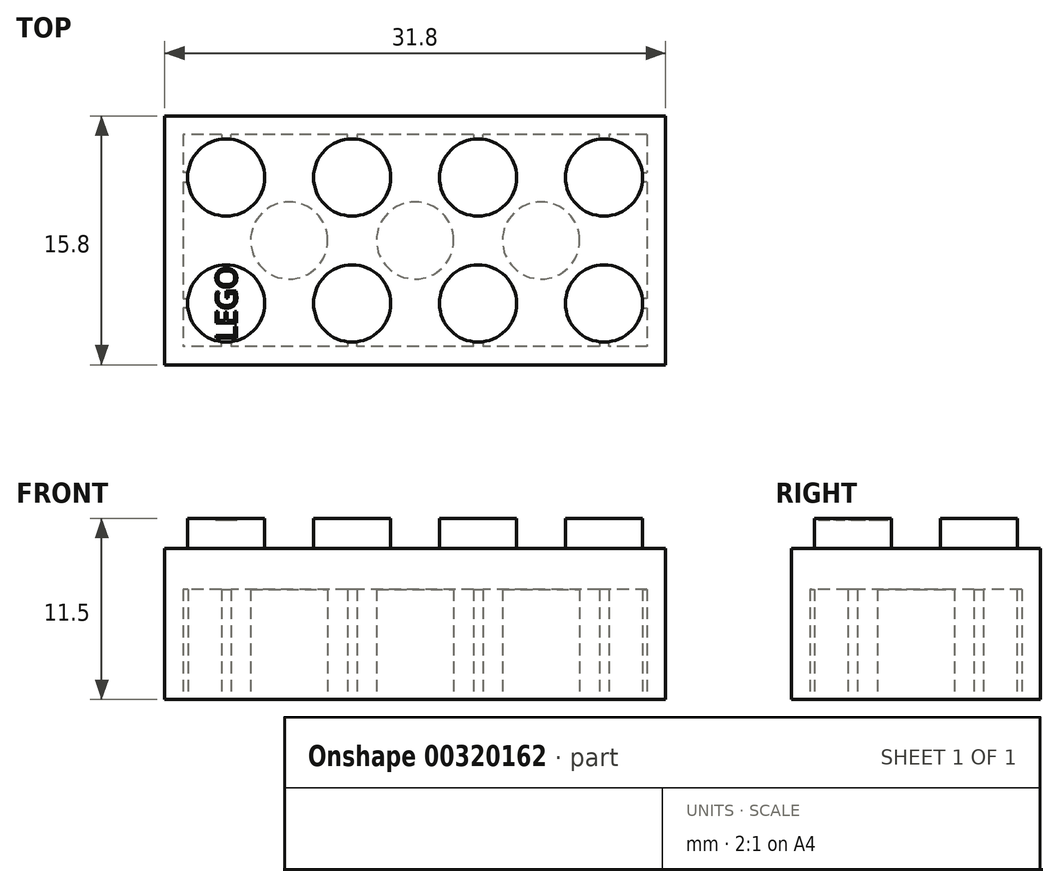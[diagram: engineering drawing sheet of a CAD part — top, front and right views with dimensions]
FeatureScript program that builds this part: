
annotation { "Feature Type Name" : "Feature", "Feature Type Description" : "" }
export const myFeature = defineFeature(function(context is Context, id is Id, definition is map)
    precondition{}
    {
        {
            var Q0;
            Q0=qCreatedBy(makeId("Top.planeOp"),FACE);
            var sketch = newSketch(context, id + "F0", { "sketchPlane" : qUnion([Q0])});
            skLineSegment(sketch, "E0.bottom", {"start": v(0, 0) * mm, "end": v(31.8, 0) * mm});
            skLineSegment(sketch, "E0.top", {"start": v(0, 15.8) * mm, "end": v(31.8, 15.8) * mm});
            skLineSegment(sketch, "E0.left", {"start": v(0, 0) * mm, "end": v(0, 15.8) * mm});
            skLineSegment(sketch, "E0.right", {"start": v(31.8, 0) * mm, "end": v(31.8, 15.8) * mm});
            skCircle(sketch, "E1", {"center": v(3.9, 11.9) * mm, "radius": 1.3 * mm, "construction": true});
            skLineSegment(sketch, "E2.bottom", {"start": v(-0.1, 15.9) * mm, "end": v(31.9, 15.9) * mm, "construction": true});
            skLineSegment(sketch, "E2.top", {"start": v(-0.1, -0.1) * mm, "end": v(31.9, -0.1) * mm, "construction": true});
            skLineSegment(sketch, "E2.left", {"start": v(-0.1, 15.9) * mm, "end": v(-0.1, -0.1) * mm, "construction": true});
            skLineSegment(sketch, "E2.right", {"start": v(31.9, 15.9) * mm, "end": v(31.9, -0.1) * mm, "construction": true});
            skLineSegment(sketch, "E3", {"start": v(15.5, 15.9) * mm, "end": v(15.5, -0.1) * mm, "construction": true});
            skLineSegment(sketch, "E4", {"start": v(16.3, -0.1) * mm, "end": v(16.3, 15.9) * mm, "construction": true});
            skLineSegment(sketch, "E5", {"start": v(15.5, 7.9) * mm, "end": v(16.3, 7.9) * mm, "construction": true});
            skCircle(sketch, "E6", {"center": v(15.9, 7.9) * mm, "radius": 3.2 * mm, "construction": true});
            skPoint(sketch, "E7", {"position": v(15.9, -0.1) * mm});
            skLineSegment(sketch, "E8", {"start": v(31.8, 7.9) * mm, "end": v(31.9, 7.9) * mm, "construction": true});
            skLineSegment(sketch, "E9", {"start": v(15.9, 15.9) * mm, "end": v(15.9, 15.8) * mm, "construction": true});
            skCircle(sketch, "E10", {"center": v(15.9, 7.9) * mm, "radius": 2.45 * mm, "construction": true});
            skCircle(sketch, "E11", {"center": v(3.9, 11.9) * mm, "radius": 2.45 * mm, "construction": true});
            skLineSegment(sketch, "E12", {"start": v(7.9, 15.9) * mm, "end": v(7.9, 7.9) * mm, "construction": true});
            skLineSegment(sketch, "E13", {"start": v(23.9, 15.9) * mm, "end": v(23.9, -0.1) * mm, "construction": true});
            skLineSegment(sketch, "E14", {"start": v(-0.1, 7.9) * mm, "end": v(7.9, 7.9) * mm, "construction": true});
            skLineSegment(sketch, "E15", {"start": v(7.9, 7.9) * mm, "end": v(15.9, 7.9) * mm, "construction": true});
            skLineSegment(sketch, "E16", {"start": v(23.9, 7.9) * mm, "end": v(15.9, 7.9) * mm, "construction": true});
            skLineSegment(sketch, "E17", {"start": v(23.9, 7.9) * mm, "end": v(31.9, 7.9) * mm, "construction": true});
            skPoint(sketch, "E18", {"position": v(0, 7.9) * mm});
            skPoint(sketch, "E19", {"position": v(3.9, 7.9) * mm});
            skLineSegment(sketch, "E20", {"start": v(7.9, 7.9) * mm, "end": v(7.9, -0.1) * mm, "construction": true});
            skPoint(sketch, "E21", {"position": v(7.9, 11.9) * mm});
            skCircle(sketch, "E22", {"center": v(7.9, 7.9) * mm, "radius": 3.2 * mm, "construction": true});
            skCircle(sketch, "E23", {"center": v(7.9, 7.9) * mm, "radius": 2.45 * mm, "construction": true});
            skCircle(sketch, "E24", {"center": v(23.9, 7.9) * mm, "radius": 3.2 * mm, "construction": true});
            skCircle(sketch, "E25", {"center": v(23.9, 7.9) * mm, "radius": 2.45 * mm, "construction": true});
            skLineSegment(sketch, "E26.bottom", {"start": v(30.63, 14.63) * mm, "end": v(1.17, 14.63) * mm, "construction": true});
            skLineSegment(sketch, "E26.top", {"start": v(30.63, 1.17) * mm, "end": v(1.17, 1.17) * mm, "construction": true});
            skLineSegment(sketch, "E26.left", {"start": v(30.63, 14.63) * mm, "end": v(30.63, 1.17) * mm, "construction": true});
            skLineSegment(sketch, "E26.right", {"start": v(1.17, 14.63) * mm, "end": v(1.17, 1.17) * mm, "construction": true});
            skLineSegment(sketch, "E27", {"start": v(3.6, 14.63) * mm, "end": v(3.6, 14.33) * mm, "construction": true});
            skLineSegment(sketch, "E28", {"start": v(3.6, 14.33) * mm, "end": v(4.2, 14.33) * mm, "construction": true});
            skLineSegment(sketch, "E29", {"start": v(4.2, 14.33) * mm, "end": v(4.2, 14.63) * mm, "construction": true});
            skLineSegment(sketch, "E30", {"start": v(1.17, 11.6) * mm, "end": v(1.47, 11.6) * mm, "construction": true});
            skLineSegment(sketch, "E31", {"start": v(1.47, 11.6) * mm, "end": v(1.47, 12.2) * mm, "construction": true});
            skLineSegment(sketch, "E32", {"start": v(1.47, 12.2) * mm, "end": v(1.17, 12.2) * mm, "construction": true});
            skCircle(sketch, "E33.MirrorC", {"center": v(11.9, 11.9) * mm, "radius": 2.45 * mm, "construction": true});
            skCircle(sketch, "E34.MirrorC", {"center": v(11.9, 11.9) * mm, "radius": 1.3 * mm, "construction": true});
            skCircle(sketch, "E35.MirrorC", {"center": v(3.9, 3.9) * mm, "radius": 2.45 * mm, "construction": true});
            skCircle(sketch, "E36.MirrorC", {"center": v(3.9, 3.9) * mm, "radius": 1.3 * mm, "construction": true});
            skCircle(sketch, "E37.MirrorC", {"center": v(11.9, 3.9) * mm, "radius": 2.45 * mm, "construction": true});
            skCircle(sketch, "E38.MirrorC", {"center": v(11.9, 3.9) * mm, "radius": 1.3 * mm, "construction": true});
            skLineSegment(sketch, "E39", {"start": v(15.9, 15.8) * mm, "end": v(15.9, -0.1) * mm, "construction": true});
            skCircle(sketch, "E40.MirrorC", {"center": v(19.9, 3.9) * mm, "radius": 2.45 * mm, "construction": true});
            skCircle(sketch, "E41.MirrorC", {"center": v(19.9, 3.9) * mm, "radius": 1.3 * mm, "construction": true});
            skCircle(sketch, "E42.MirrorC", {"center": v(19.9, 11.9) * mm, "radius": 1.3 * mm, "construction": true});
            skCircle(sketch, "E43.MirrorC", {"center": v(19.9, 11.9) * mm, "radius": 2.45 * mm, "construction": true});
            skCircle(sketch, "E44.MirrorC", {"center": v(27.9, 11.9) * mm, "radius": 2.45 * mm, "construction": true});
            skCircle(sketch, "E45.MirrorC", {"center": v(27.9, 11.9) * mm, "radius": 1.3 * mm, "construction": true});
            skCircle(sketch, "E46.MirrorC", {"center": v(27.9, 3.9) * mm, "radius": 2.45 * mm, "construction": true});
            skCircle(sketch, "E47.MirrorC", {"center": v(27.9, 3.9) * mm, "radius": 1.3 * mm, "construction": true});
            skLineSegment(sketch, "E48.MirrorCS", {"start": v(1.47, 3.6) * mm, "end": v(1.17, 3.6) * mm, "construction": true});
            skLineSegment(sketch, "E49.MirrorCS", {"start": v(1.17, 4.2) * mm, "end": v(1.47, 4.2) * mm, "construction": true});
            skLineSegment(sketch, "E50.MirrorCS", {"start": v(1.47, 4.2) * mm, "end": v(1.47, 3.6) * mm, "construction": true});
            skLineSegment(sketch, "E51.MirrorCS", {"start": v(3.6, 1.17) * mm, "end": v(3.6, 1.47) * mm, "construction": true});
            skLineSegment(sketch, "E52.MirrorCS", {"start": v(4.2, 1.47) * mm, "end": v(4.2, 1.17) * mm, "construction": true});
            skLineSegment(sketch, "E53.MirrorCS", {"start": v(3.6, 1.47) * mm, "end": v(4.2, 1.47) * mm, "construction": true});
            skLineSegment(sketch, "E54.MirrorCS", {"start": v(11.6, 14.33) * mm, "end": v(11.6, 14.63) * mm, "construction": true});
            skLineSegment(sketch, "E55.MirrorCS", {"start": v(12.2, 14.63) * mm, "end": v(12.2, 14.33) * mm, "construction": true});
            skLineSegment(sketch, "E56.MirrorCS", {"start": v(12.2, 14.33) * mm, "end": v(11.6, 14.33) * mm, "construction": true});
            skLineSegment(sketch, "E57.MirrorCS", {"start": v(12.2, 1.17) * mm, "end": v(12.2, 1.47) * mm, "construction": true});
            skLineSegment(sketch, "E58.MirrorCS", {"start": v(11.6, 1.47) * mm, "end": v(11.6, 1.17) * mm, "construction": true});
            skLineSegment(sketch, "E59.MirrorCS", {"start": v(12.2, 1.47) * mm, "end": v(11.6, 1.47) * mm, "construction": true});
            skLineSegment(sketch, "E60.MirrorCS", {"start": v(19.6, 14.63) * mm, "end": v(19.6, 14.33) * mm, "construction": true});
            skLineSegment(sketch, "E61.MirrorCS", {"start": v(19.6, 14.33) * mm, "end": v(20.2, 14.33) * mm, "construction": true});
            skLineSegment(sketch, "E62.MirrorCS", {"start": v(20.2, 14.33) * mm, "end": v(20.2, 14.63) * mm, "construction": true});
            skLineSegment(sketch, "E63.MirrorCS", {"start": v(28.2, 14.63) * mm, "end": v(28.2, 14.33) * mm, "construction": true});
            skLineSegment(sketch, "E64.MirrorCS", {"start": v(27.6, 14.33) * mm, "end": v(27.6, 14.63) * mm, "construction": true});
            skLineSegment(sketch, "E65.MirrorCS", {"start": v(28.2, 14.33) * mm, "end": v(27.6, 14.33) * mm, "construction": true});
            skLineSegment(sketch, "E66.MirrorCS", {"start": v(30.33, 12.2) * mm, "end": v(30.63, 12.2) * mm, "construction": true});
            skLineSegment(sketch, "E67.MirrorCS", {"start": v(30.63, 11.6) * mm, "end": v(30.33, 11.6) * mm, "construction": true});
            skLineSegment(sketch, "E68.MirrorCS", {"start": v(30.33, 11.6) * mm, "end": v(30.33, 12.2) * mm, "construction": true});
            skLineSegment(sketch, "E69.MirrorCS", {"start": v(30.33, 3.6) * mm, "end": v(30.63, 3.6) * mm, "construction": true});
            skLineSegment(sketch, "E70.MirrorCS", {"start": v(30.63, 4.2) * mm, "end": v(30.33, 4.2) * mm, "construction": true});
            skLineSegment(sketch, "E71.MirrorCS", {"start": v(30.33, 4.2) * mm, "end": v(30.33, 3.6) * mm, "construction": true});
            skLineSegment(sketch, "E72.MirrorCS", {"start": v(28.2, 1.17) * mm, "end": v(28.2, 1.47) * mm, "construction": true});
            skLineSegment(sketch, "E73.MirrorCS", {"start": v(27.6, 1.47) * mm, "end": v(27.6, 1.17) * mm, "construction": true});
            skLineSegment(sketch, "E74.MirrorCS", {"start": v(28.2, 1.47) * mm, "end": v(27.6, 1.47) * mm, "construction": true});
            skLineSegment(sketch, "E75.MirrorCS", {"start": v(20.2, 1.47) * mm, "end": v(20.2, 1.17) * mm, "construction": true});
            skLineSegment(sketch, "E76.MirrorCS", {"start": v(19.6, 1.17) * mm, "end": v(19.6, 1.47) * mm, "construction": true});
            skLineSegment(sketch, "E77.MirrorCS", {"start": v(19.6, 1.47) * mm, "end": v(20.2, 1.47) * mm, "construction": true});
            skSolve(sketch);
        }
        {
            var Q0;
            Q0=makeQuery(id+"F0.imprint","IMPRINT",FACE,{"disambiguationData":[TD([[makeQuery(id+"F0.imprint","IMPRINT",EDGE,{"derivedFrom":sQuery(id+"F0.wireOp",EDGE,"E0.bottom")}),1.0]])]});
            extrude(context, id + "F1", {"entities" : qUnion([Q0]), "depth" : 9.6 * mm});
        }
        {
            var Q0;
            Q0=makeQuery(id+"F1.opExtrude","CAP_FACE",FACE,{"disambiguationData":[OSD([sQuery(id+"F0.wireOp",EDGE,"E0.bottom"),sQuery(id+"F0.wireOp",EDGE,"E0.top"),sQuery(id+"F0.wireOp",EDGE,"E0.left"),sQuery(id+"F0.wireOp",EDGE,"E0.right")])],"isStart":false});
            var sketch = newSketch(context, id + "F2", { "sketchPlane" : qUnion([Q0])});
            skCircle(sketch, "E78.0", {"center": v(3.9, 3.9) * mm, "radius": 2.45 * mm});
            skCircle(sketch, "E79.0", {"center": v(3.9, 11.9) * mm, "radius": 2.45 * mm});
            skCircle(sketch, "E80.0", {"center": v(11.9, 3.9) * mm, "radius": 2.45 * mm});
            skCircle(sketch, "E81.0", {"center": v(11.9, 11.9) * mm, "radius": 2.45 * mm});
            skCircle(sketch, "E82.0", {"center": v(19.9, 3.9) * mm, "radius": 2.45 * mm});
            skCircle(sketch, "E83.0", {"center": v(19.9, 11.9) * mm, "radius": 2.45 * mm});
            skCircle(sketch, "E84.0", {"center": v(27.9, 3.9) * mm, "radius": 2.45 * mm});
            skCircle(sketch, "E85.0", {"center": v(27.9, 11.9) * mm, "radius": 2.45 * mm});
            skSolve(sketch);
        }
        {
            var Q0;
            Q0=qSketchRegion(id+"F2",true);
            extrude(context, id + "F3", {"entities" : qUnion([Q0]), "operationType" : NewBodyOperationType.ADD, "depth" : 1.9 * mm});
        }
        {
            var Q0;
            Q0=makeQuery(id+"F1.opExtrude","CAP_FACE",FACE,{"disambiguationData":[OSD([sQuery(id+"F0.wireOp",EDGE,"E0.bottom"),sQuery(id+"F0.wireOp",EDGE,"E0.top"),sQuery(id+"F0.wireOp",EDGE,"E0.left"),sQuery(id+"F0.wireOp",EDGE,"E0.right")])],"isStart":true});
            var sketch = newSketch(context, id + "F4", { "sketchPlane" : qUnion([Q0])});
            skLineSegment(sketch, "E86.0", {"start": v(30.63, -1.17) * mm, "end": v(1.17, -1.17) * mm});
            skLineSegment(sketch, "E87.0", {"start": v(3.6, -1.17) * mm, "end": v(3.6, -1.47) * mm});
            skLineSegment(sketch, "E88.0", {"start": v(4.2, -1.47) * mm, "end": v(4.2, -1.17) * mm});
            skLineSegment(sketch, "E89.0", {"start": v(3.6, -1.47) * mm, "end": v(4.2, -1.47) * mm});
            skLineSegment(sketch, "E90.0", {"start": v(1.17, -14.63) * mm, "end": v(1.17, -1.17) * mm});
            skLineSegment(sketch, "E91.0", {"start": v(1.17, -4.2) * mm, "end": v(1.47, -4.2) * mm});
            skLineSegment(sketch, "E92.0", {"start": v(1.47, -3.6) * mm, "end": v(1.17, -3.6) * mm});
            skLineSegment(sketch, "E93.0", {"start": v(1.47, -4.2) * mm, "end": v(1.47, -3.6) * mm});
            skLineSegment(sketch, "E94.0", {"start": v(1.17, -11.6) * mm, "end": v(1.47, -11.6) * mm});
            skLineSegment(sketch, "E95.0", {"start": v(1.47, -12.2) * mm, "end": v(1.17, -12.2) * mm});
            skLineSegment(sketch, "E96.0", {"start": v(1.47, -11.6) * mm, "end": v(1.47, -12.2) * mm});
            skLineSegment(sketch, "E97.0", {"start": v(4.2, -14.33) * mm, "end": v(4.2, -14.63) * mm});
            skLineSegment(sketch, "E98.0", {"start": v(3.6, -14.63) * mm, "end": v(3.6, -14.33) * mm});
            skLineSegment(sketch, "E99.0", {"start": v(3.6, -14.33) * mm, "end": v(4.2, -14.33) * mm});
            skLineSegment(sketch, "E100.0", {"start": v(30.63, -14.63) * mm, "end": v(1.17, -14.63) * mm});
            skLineSegment(sketch, "E101.0", {"start": v(11.6, -1.47) * mm, "end": v(11.6, -1.17) * mm});
            skLineSegment(sketch, "E102.0", {"start": v(12.2, -1.17) * mm, "end": v(12.2, -1.47) * mm});
            skLineSegment(sketch, "E103.0", {"start": v(12.2, -1.47) * mm, "end": v(11.6, -1.47) * mm});
            skLineSegment(sketch, "E104.0", {"start": v(19.6, -1.47) * mm, "end": v(20.2, -1.47) * mm});
            skLineSegment(sketch, "E105.0", {"start": v(19.6, -1.17) * mm, "end": v(19.6, -1.47) * mm});
            skLineSegment(sketch, "E106.0", {"start": v(20.2, -1.47) * mm, "end": v(20.2, -1.17) * mm});
            skLineSegment(sketch, "E107.0", {"start": v(28.2, -1.47) * mm, "end": v(27.6, -1.47) * mm});
            skLineSegment(sketch, "E108.0", {"start": v(27.6, -1.47) * mm, "end": v(27.6, -1.17) * mm});
            skLineSegment(sketch, "E109.0", {"start": v(28.2, -1.17) * mm, "end": v(28.2, -1.47) * mm});
            skLineSegment(sketch, "E110.0", {"start": v(30.33, -3.6) * mm, "end": v(30.63, -3.6) * mm});
            skLineSegment(sketch, "E111.0", {"start": v(30.33, -4.2) * mm, "end": v(30.33, -3.6) * mm});
            skLineSegment(sketch, "E112.0", {"start": v(30.63, -4.2) * mm, "end": v(30.33, -4.2) * mm});
            skLineSegment(sketch, "E113.0", {"start": v(30.63, -14.63) * mm, "end": v(30.63, -1.17) * mm});
            skLineSegment(sketch, "E114.0", {"start": v(30.63, -11.6) * mm, "end": v(30.33, -11.6) * mm});
            skLineSegment(sketch, "E115.0", {"start": v(30.33, -11.6) * mm, "end": v(30.33, -12.2) * mm});
            skLineSegment(sketch, "E116.0", {"start": v(30.33, -12.2) * mm, "end": v(30.63, -12.2) * mm});
            skLineSegment(sketch, "E117.0", {"start": v(28.2, -14.33) * mm, "end": v(27.6, -14.33) * mm});
            skLineSegment(sketch, "E118.0", {"start": v(28.2, -14.63) * mm, "end": v(28.2, -14.33) * mm});
            skLineSegment(sketch, "E119.0", {"start": v(27.6, -14.33) * mm, "end": v(27.6, -14.63) * mm});
            skLineSegment(sketch, "E120.0", {"start": v(19.6, -14.33) * mm, "end": v(20.2, -14.33) * mm});
            skLineSegment(sketch, "E121.0", {"start": v(20.2, -14.33) * mm, "end": v(20.2, -14.63) * mm});
            skLineSegment(sketch, "E122.0", {"start": v(19.6, -14.63) * mm, "end": v(19.6, -14.33) * mm});
            skLineSegment(sketch, "E123.0", {"start": v(12.2, -14.63) * mm, "end": v(12.2, -14.33) * mm});
            skLineSegment(sketch, "E124.0", {"start": v(11.6, -14.33) * mm, "end": v(11.6, -14.63) * mm});
            skLineSegment(sketch, "E125.0", {"start": v(12.2, -14.33) * mm, "end": v(11.6, -14.33) * mm});
            skCircle(sketch, "E126.0", {"center": v(7.9, -7.9) * mm, "radius": 2.45 * mm});
            skCircle(sketch, "E127.0", {"center": v(7.9, -7.9) * mm, "radius": 3.2 * mm});
            skCircle(sketch, "E128.0", {"center": v(15.9, -7.9) * mm, "radius": 3.2 * mm});
            skCircle(sketch, "E129.0", {"center": v(15.9, -7.9) * mm, "radius": 2.45 * mm});
            skCircle(sketch, "E130.0", {"center": v(23.9, -7.9) * mm, "radius": 3.2 * mm});
            skCircle(sketch, "E131.0", {"center": v(23.9, -7.9) * mm, "radius": 2.45 * mm});
            skSolve(sketch);
        }
        {
            var Q0;
            {var subQ27=sQuery(id+"F4.wireOp",EDGE,"E87.0");Q0=makeQuery(id+"F4.imprint","IMPRINT",FACE,{"disambiguationData":[TD([[makeQuery(id+"F4.imprint","IMPRINT",EDGE,{"derivedFrom":subQ27}),-1.0]])]});}
            var Q1;
            Q1=makeQuery(id+"F4.imprint","IMPRINT",FACE,{"disambiguationData":[TD([[makeQuery(id+"F4.imprint","IMPRINT",EDGE,{"derivedFrom":sQuery(id+"F4.wireOp",EDGE,"E126.0")}),-1.0]])]});
            var Q2;
            Q2=makeQuery(id+"F4.imprint","IMPRINT",FACE,{"disambiguationData":[TD([[makeQuery(id+"F4.imprint","IMPRINT",EDGE,{"derivedFrom":sQuery(id+"F4.wireOp",EDGE,"E129.0")}),-1.0]])]});
            var Q3;
            Q3=makeQuery(id+"F4.imprint","IMPRINT",FACE,{"disambiguationData":[TD([[makeQuery(id+"F4.imprint","IMPRINT",EDGE,{"derivedFrom":sQuery(id+"F4.wireOp",EDGE,"E131.0")}),-1.0]])]});
            extrude(context, id + "F5", {"entities" : qUnion([Q0, Q1, Q2, Q3]), "operationType" : NewBodyOperationType.REMOVE, "oppositeDirection" : true, "depth" : 7 * mm});
        }
        {
            var Q0;
            Q0=makeQuery(id+"F3.opExtrude","CAP_FACE",FACE,{"disambiguationData":[OSD([sQuery(id+"F2.wireOp",EDGE,"E78.0")])],"isStart":false});
            var sketch = newSketch(context, id + "F6", { "sketchPlane" : qUnion([Q0])});
            skText(sketch, "E132", { "text": "LEGO", "fontName": "OpenSans-Regular.ttf"});
            skCircle(sketch, "E133.0", {"center": v(3.9, 3.9) * mm, "radius": 2.45 * mm, "construction": true});
            const initialGuessF6  = {"E132": [0.00456, 0.00154, 0, 1, 0.00131]};
            skSetInitialGuess(sketch, initialGuessF6);
            skSolve(sketch);
        }
        {
            var Q0;
            Q0=makeQuery(id+"F6.imprint","IMPRINT",FACE,{"disambiguationData":[TD([[makeQuery(id+"F6.imprint","IMPRINT",EDGE,{"derivedFrom":sQuery(id+"F6.wireOp",EDGE,"E132.sketch_text.stroke-38")}),-1.0]])]});
            var Q1;
            Q1=makeQuery(id+"F6.imprint","IMPRINT",FACE,{"disambiguationData":[TD([[makeQuery(id+"F6.imprint","IMPRINT",EDGE,{"derivedFrom":sQuery(id+"F6.wireOp",EDGE,"E132.sketch_text.stroke-18")}),-1.0]])]});
            var Q2;
            Q2=makeQuery(id+"F6.imprint","IMPRINT",FACE,{"disambiguationData":[TD([[makeQuery(id+"F6.imprint","IMPRINT",EDGE,{"derivedFrom":sQuery(id+"F6.wireOp",EDGE,"E132.sketch_text.stroke-6")}),-1.0]])]});
            var Q3;
            Q3=makeQuery(id+"F6.imprint","IMPRINT",FACE,{"disambiguationData":[TD([[makeQuery(id+"F6.imprint","IMPRINT",EDGE,{"derivedFrom":sQuery(id+"F6.wireOp",EDGE,"E132.sketch_text.stroke-0")}),-1.0]])]});
            extrude(context, id + "F7", {"entities" : qUnion([Q0, Q1, Q2, Q3]), "operationType" : NewBodyOperationType.REMOVE, "oppositeDirection" : true, "depth" : .1 * mm});
        }
    });
